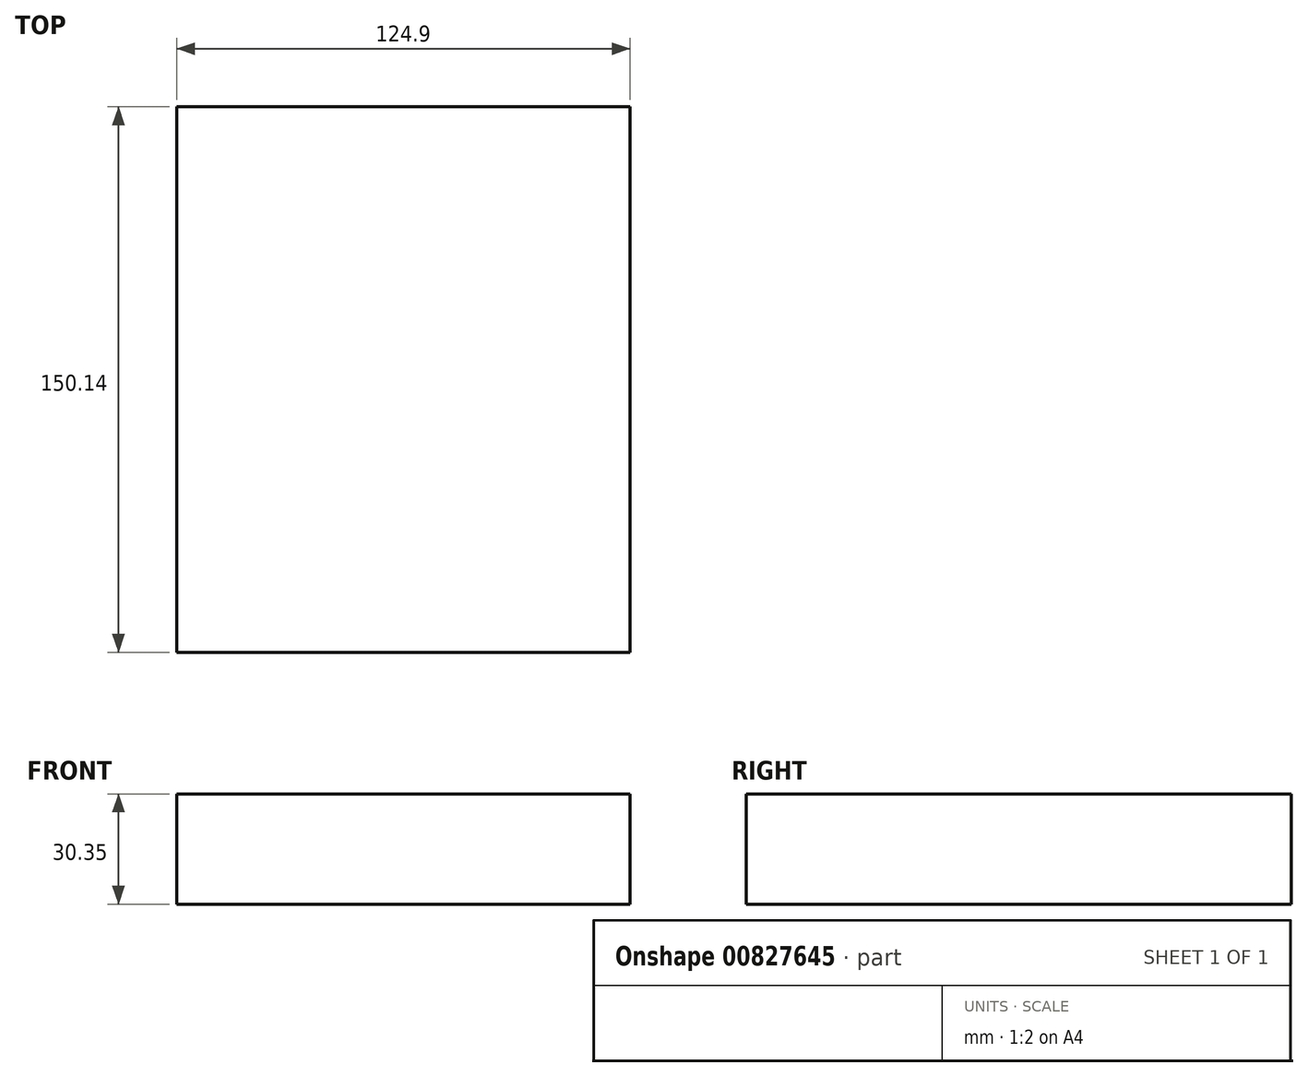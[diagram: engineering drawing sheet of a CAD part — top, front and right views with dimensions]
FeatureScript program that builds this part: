
annotation { "Feature Type Name" : "Feature", "Feature Type Description" : "" }
export const myFeature = defineFeature(function(context is Context, id is Id, definition is map)
    precondition{}
    {
        {
            var Q0;
            Q0=qCreatedBy(makeId("Top.planeOp"),FACE);
            var sketch = newSketch(context, id + "F0", { "sketchPlane" : qUnion([Q0])});
            skLineSegment(sketch, "E0", {"start": v(-18.9, 77.51) * mm, "end": v(-18.9, -72.63) * mm});
            skLineSegment(sketch, "E1", {"start": v(-18.9, -72.63) * mm, "end": v(106.01, -72.63) * mm});
            skLineSegment(sketch, "E2", {"start": v(106.01, -72.63) * mm, "end": v(106.01, 77.51) * mm});
            skLineSegment(sketch, "E3", {"start": v(106.01, 77.51) * mm, "end": v(-18.9, 77.51) * mm});
            skSolve(sketch);
        }
        {
            var Q0;
            Q0 = qSketchRegion(id + "F0", true);
            extrude(context, id + "F1", {"entities" : qUnion([Q0]), "depth" : 30.35 * mm, "offsetDistance" : 25.4 * mm});
        }
    });
